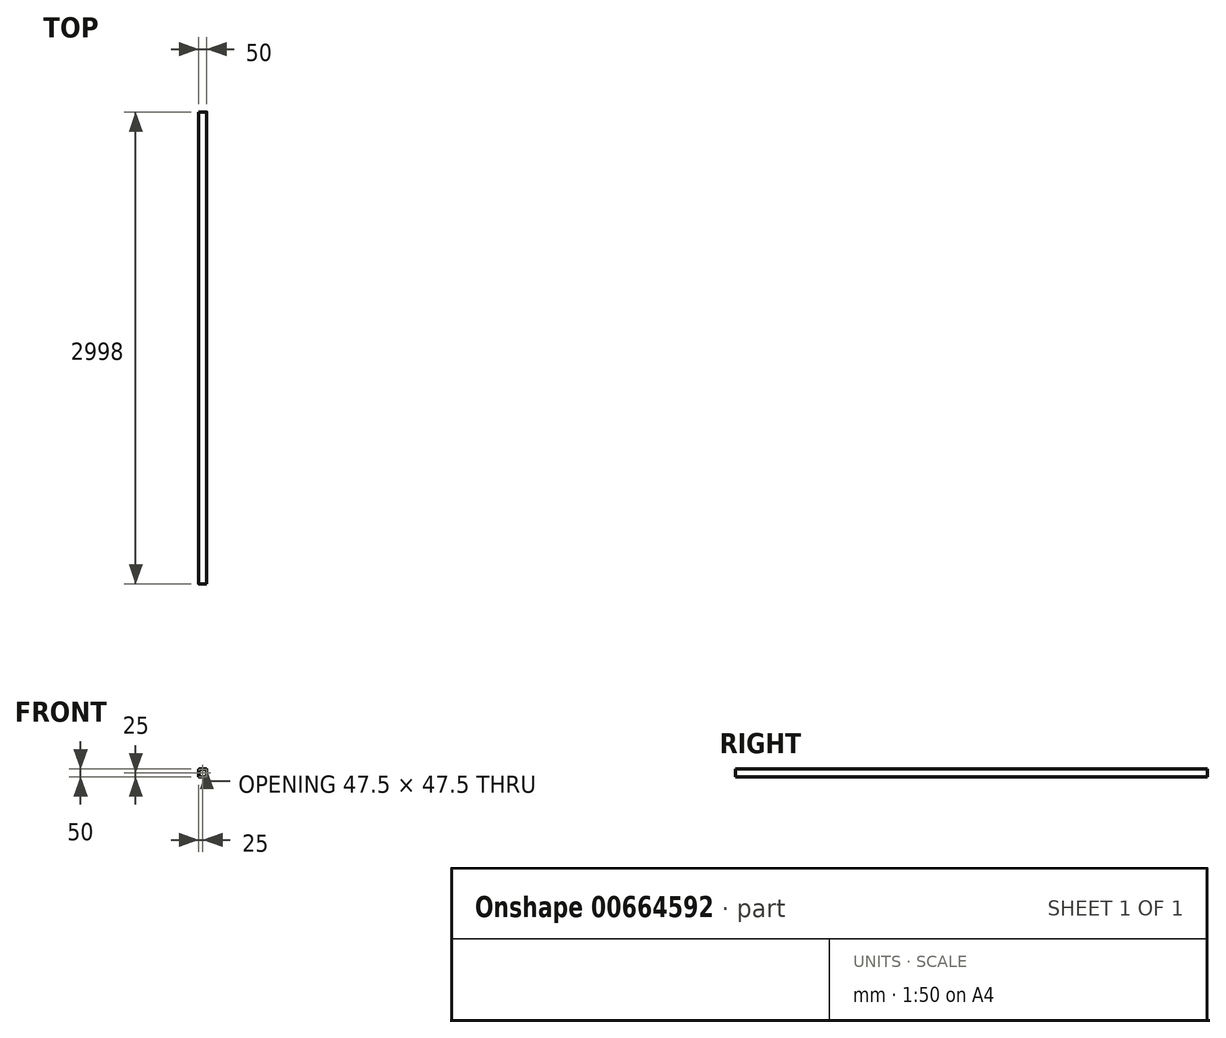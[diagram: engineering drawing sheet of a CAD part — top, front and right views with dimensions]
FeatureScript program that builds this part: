
annotation { "Feature Type Name" : "Feature", "Feature Type Description" : "" }
export const myFeature = defineFeature(function(context is Context, id is Id, definition is map)
    precondition{}
    {
        {
            var Q0;
            Q0=qCreatedBy(makeId("Front.planeOp"),FACE);
            var sketch = newSketch(context, id + "F0", { "sketchPlane" : qUnion([Q0])});
            skLineSegment(sketch, "E0.bottom", {"start": v(23, 25) * mm, "end": v(-23, 25) * mm});
            skLineSegment(sketch, "E0.top", {"start": v(23, -25) * mm, "end": v(-23, -25) * mm});
            skLineSegment(sketch, "E0.left", {"start": v(25, 23) * mm, "end": v(25, -23) * mm});
            skLineSegment(sketch, "E0.right", {"start": v(-25, 23) * mm, "end": v(-25, -23) * mm});
            skPoint(sketch, "E0.middle", {"position": v(0, 0) * mm});
            skLineSegment(sketch, "E1.0", {"start": v(21.75, 23.75) * mm, "end": v(-21.75, 23.75) * mm});
            skLineSegment(sketch, "E1.1", {"start": v(23.75, 21.75) * mm, "end": v(23.75, -21.75) * mm});
            skLineSegment(sketch, "E1.2", {"start": v(21.75, -23.75) * mm, "end": v(-21.75, -23.75) * mm});
            skLineSegment(sketch, "E1.3", {"start": v(-23.75, 21.75) * mm, "end": v(-23.75, -21.75) * mm});
            skPoint(sketch, "E2.visualSharp", {"position": v(-23.75, 23.75) * mm});
            skArc(sketch, "E2.filletArc", {"start": v(-21.75, 23.75) * mm, "mid": v(-23.16, 23.16) * mm, "end": v(-23.75, 21.75) * mm});
            skPoint(sketch, "E3.visualSharp", {"position": v(23.75, 23.75) * mm});
            skArc(sketch, "E3.filletArc", {"start": v(23.75, 21.75) * mm, "mid": v(23.16, 23.16) * mm, "end": v(21.75, 23.75) * mm});
            skPoint(sketch, "E4.visualSharp", {"position": v(23.75, -23.75) * mm});
            skArc(sketch, "E4.filletArc", {"start": v(21.75, -23.75) * mm, "mid": v(23.16, -23.16) * mm, "end": v(23.75, -21.75) * mm});
            skPoint(sketch, "E5.visualSharp", {"position": v(-23.75, -23.75) * mm});
            skArc(sketch, "E5.filletArc", {"start": v(-23.75, -21.75) * mm, "mid": v(-23.16, -23.16) * mm, "end": v(-21.75, -23.75) * mm});
            skPoint(sketch, "E6.visualSharp", {"position": v(-25, -25) * mm});
            skArc(sketch, "E6.filletArc", {"start": v(-25, -23) * mm, "mid": v(-24.41, -24.41) * mm, "end": v(-23, -25) * mm});
            skPoint(sketch, "E7.visualSharp", {"position": v(-25, 25) * mm});
            skArc(sketch, "E7.filletArc", {"start": v(-23, 25) * mm, "mid": v(-24.41, 24.41) * mm, "end": v(-25, 23) * mm});
            skPoint(sketch, "E8.visualSharp", {"position": v(25, 25) * mm});
            skArc(sketch, "E8.filletArc", {"start": v(25, 23) * mm, "mid": v(24.41, 24.41) * mm, "end": v(23, 25) * mm});
            skPoint(sketch, "E9.visualSharp", {"position": v(25, -25) * mm});
            skArc(sketch, "E9.filletArc", {"start": v(23, -25) * mm, "mid": v(24.41, -24.41) * mm, "end": v(25, -23) * mm});
            skSolve(sketch);
        }
        {
            var Q0;
            Q0=makeQuery(id+"F0.imprint","IMPRINT",FACE,{"disambiguationData":[TD([[makeQuery(id+"F0.imprint","IMPRINT",EDGE,{"derivedFrom":sQuery(id+"F0.wireOp",EDGE,"E0.bottom")}),1.0]])]});
            extrude(context, id + "F1", {"entities" : qUnion([Q0]), "endBound" : BoundingType.SYMMETRIC, "depth" : 3000 * mm - 2 * mm, "offsetDistance" : 25 * mm});
        }
    });
